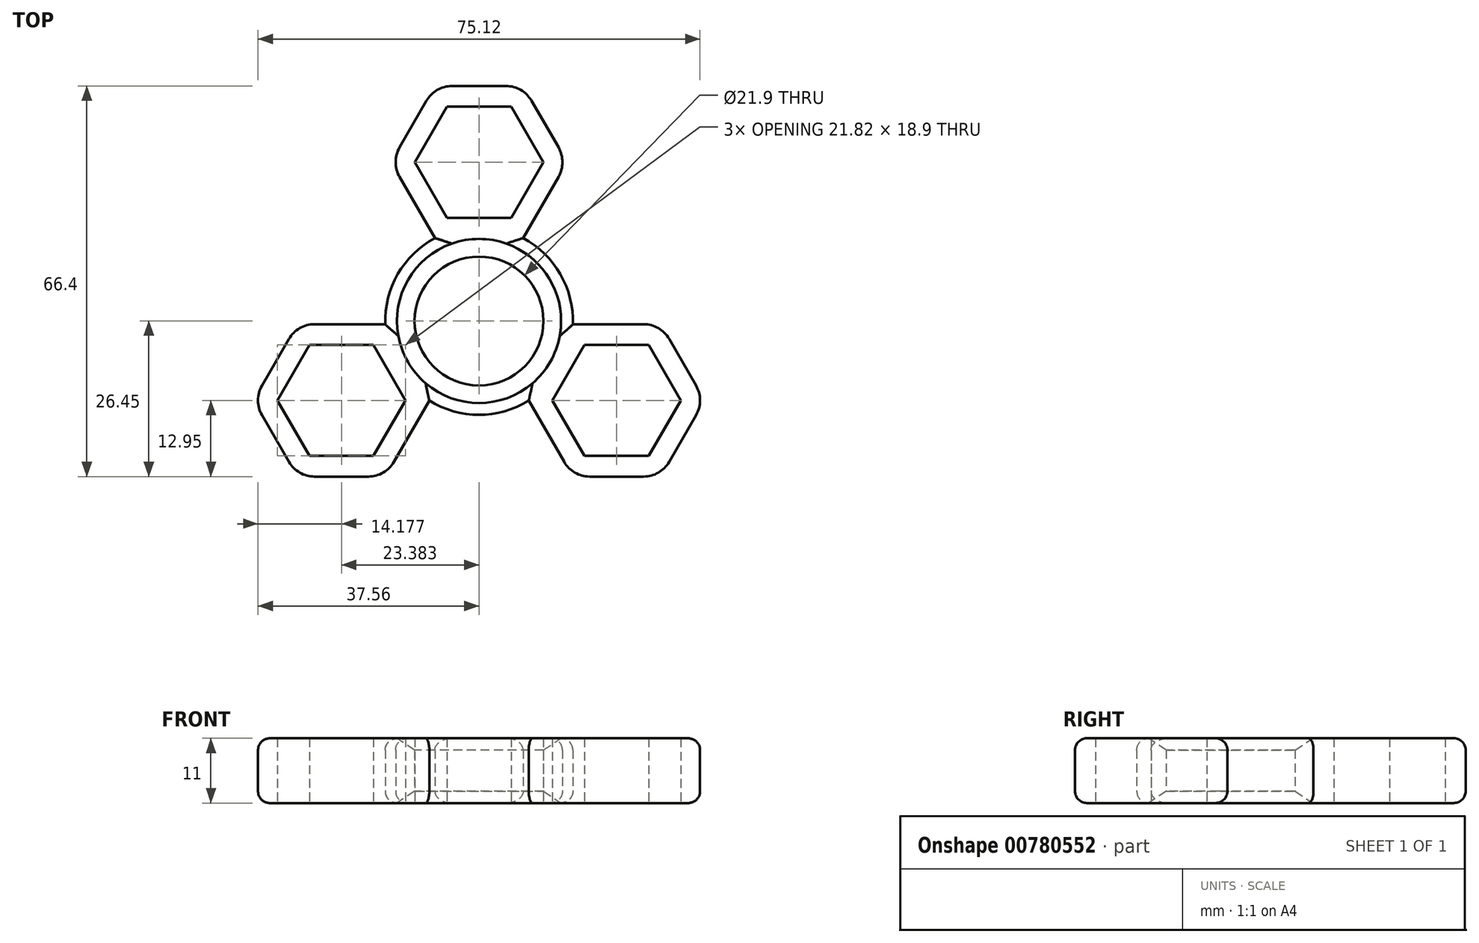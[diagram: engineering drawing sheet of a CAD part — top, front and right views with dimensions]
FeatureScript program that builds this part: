
annotation { "Feature Type Name" : "Feature", "Feature Type Description" : "" }
export const myFeature = defineFeature(function(context is Context, id is Id, definition is map)
    precondition{}
    {
        {
            var Q0;
            Q0=qCreatedBy(makeId("Top.planeOp"),FACE);
            var sketch = newSketch(context, id + "F0", { "sketchPlane" : qUnion([Q0])});
            skCircle(sketch, "E0", {"center": v(0, 0) * mm, "radius": 10.95 * mm});
            skCircle(sketch, "E1.cCircle", {"center": v(0, 0) * mm, "radius": 13.5 * mm, "construction": true});
            skLineSegment(sketch, "E1.0", {"start": v(0, 27) * mm, "end": v(23.38, -13.5) * mm, "construction": true});
            skLineSegment(sketch, "E1.1", {"start": v(23.38, -13.5) * mm, "end": v(-23.38, -13.5) * mm, "construction": true});
            skLineSegment(sketch, "E1.2", {"start": v(-23.38, -13.5) * mm, "end": v(0, 27) * mm, "construction": true});
            skPoint(sketch, "E1.0.midPoint", {"position": v(11.7, 6.75) * mm});
            skLineSegment(sketch, "E2", {"start": v(0, 0) * mm, "end": v(-23.38, -13.5) * mm, "construction": true});
            skLineSegment(sketch, "E3", {"start": v(0, 0) * mm, "end": v(23.38, -13.5) * mm, "construction": true});
            skLineSegment(sketch, "E4", {"start": v(0, 0) * mm, "end": v(0, 27) * mm, "construction": true});
            skCircle(sketch, "E5.cCircle", {"center": v(0, 27) * mm, "radius": 9.45 * mm, "construction": true});
            skLineSegment(sketch, "E5.0", {"start": v(-5.46, 36.45) * mm, "end": v(5.46, 36.45) * mm});
            skLineSegment(sketch, "E5.1", {"start": v(5.46, 36.45) * mm, "end": v(10.91, 27) * mm});
            skLineSegment(sketch, "E5.2", {"start": v(10.91, 27) * mm, "end": v(5.46, 17.55) * mm});
            skLineSegment(sketch, "E5.3", {"start": v(5.46, 17.55) * mm, "end": v(-5.46, 17.55) * mm});
            skLineSegment(sketch, "E5.4", {"start": v(-5.46, 17.55) * mm, "end": v(-10.91, 27) * mm});
            skLineSegment(sketch, "E5.5", {"start": v(-10.91, 27) * mm, "end": v(-5.46, 36.45) * mm});
            skPoint(sketch, "E5.0.midPoint", {"position": v(0, 36.45) * mm});
            skCircle(sketch, "E6.cCircle", {"center": v(23.38, -13.5) * mm, "radius": 9.45 * mm, "construction": true});
            skLineSegment(sketch, "E6.0", {"start": v(34.3, -13.5) * mm, "end": v(28.84, -22.95) * mm});
            skLineSegment(sketch, "E6.1", {"start": v(28.84, -22.95) * mm, "end": v(17.93, -22.95) * mm});
            skLineSegment(sketch, "E6.2", {"start": v(17.93, -22.95) * mm, "end": v(12.47, -13.5) * mm});
            skLineSegment(sketch, "E6.3", {"start": v(12.47, -13.5) * mm, "end": v(17.93, -4.05) * mm});
            skLineSegment(sketch, "E6.4", {"start": v(17.93, -4.05) * mm, "end": v(28.84, -4.05) * mm});
            skLineSegment(sketch, "E6.5", {"start": v(28.84, -4.05) * mm, "end": v(34.3, -13.5) * mm});
            skPoint(sketch, "E6.0.midPoint", {"position": v(31.57, -18.22) * mm});
            skCircle(sketch, "E7.cCircle", {"center": v(-23.38, -13.5) * mm, "radius": 9.45 * mm, "construction": true});
            skLineSegment(sketch, "E7.0", {"start": v(-28.84, -22.95) * mm, "end": v(-34.3, -13.5) * mm});
            skLineSegment(sketch, "E7.1", {"start": v(-34.3, -13.5) * mm, "end": v(-28.84, -4.05) * mm});
            skLineSegment(sketch, "E7.2", {"start": v(-28.84, -4.05) * mm, "end": v(-17.93, -4.05) * mm});
            skLineSegment(sketch, "E7.3", {"start": v(-17.93, -4.05) * mm, "end": v(-12.47, -13.5) * mm});
            skLineSegment(sketch, "E7.4", {"start": v(-12.47, -13.5) * mm, "end": v(-17.93, -22.95) * mm});
            skLineSegment(sketch, "E7.5", {"start": v(-17.93, -22.95) * mm, "end": v(-28.84, -22.95) * mm});
            skPoint(sketch, "E7.0.midPoint", {"position": v(-31.57, -18.22) * mm});
            skLineSegment(sketch, "E8.0", {"start": v(-14.95, 27) * mm, "end": v(-7.48, 39.95) * mm});
            skLineSegment(sketch, "E8.1", {"start": v(7.48, 39.95) * mm, "end": v(14.95, 27) * mm});
            skLineSegment(sketch, "E8.2", {"start": v(14.95, 27) * mm, "end": v(7.48, 14.05) * mm});
            skLineSegment(sketch, "E8.3", {"start": v(-7.48, 39.95) * mm, "end": v(7.48, 39.95) * mm});
            skLineSegment(sketch, "E8.4", {"start": v(7.48, 14.05) * mm, "end": v(-7.48, 14.05) * mm});
            skLineSegment(sketch, "E8.5", {"start": v(-7.48, 14.05) * mm, "end": v(-14.95, 27) * mm});
            skLineSegment(sketch, "E9.0", {"start": v(8.43, -13.5) * mm, "end": v(15.9, -0.55) * mm});
            skLineSegment(sketch, "E9.1", {"start": v(30.86, -0.55) * mm, "end": v(38.34, -13.5) * mm});
            skLineSegment(sketch, "E9.2", {"start": v(38.34, -13.5) * mm, "end": v(30.86, -26.45) * mm});
            skLineSegment(sketch, "E9.3", {"start": v(15.9, -0.55) * mm, "end": v(30.86, -0.55) * mm});
            skLineSegment(sketch, "E9.4", {"start": v(30.86, -26.45) * mm, "end": v(15.9, -26.45) * mm});
            skLineSegment(sketch, "E9.5", {"start": v(15.9, -26.45) * mm, "end": v(8.43, -13.5) * mm});
            skLineSegment(sketch, "E10.0", {"start": v(-38.34, -13.5) * mm, "end": v(-30.86, -0.55) * mm});
            skLineSegment(sketch, "E10.1", {"start": v(-15.9, -0.55) * mm, "end": v(-8.43, -13.5) * mm});
            skLineSegment(sketch, "E10.2", {"start": v(-8.43, -13.5) * mm, "end": v(-15.9, -26.45) * mm});
            skLineSegment(sketch, "E10.3", {"start": v(-30.86, -0.55) * mm, "end": v(-15.9, -0.55) * mm});
            skLineSegment(sketch, "E10.4", {"start": v(-15.9, -26.45) * mm, "end": v(-30.86, -26.45) * mm});
            skLineSegment(sketch, "E10.5", {"start": v(-30.86, -26.45) * mm, "end": v(-38.34, -13.5) * mm});
            skCircle(sketch, "E11.0", {"center": v(0, 0) * mm, "radius": 15.95 * mm});
            skSolve(sketch);
        }
        {
            var Q0;
            Q0=qSketchRegion(id+"F0",true);
            extrude(context, id + "F1", {"entities" : qUnion([Q0]), "depth" : 11 * mm, "offsetDistance" : 25 * mm});
        }
        {
            var Q0;
            Q0=makeQuery(id+"F1.opExtrude","CAP_EDGE",EDGE,{"disambiguationData":[OSD([sQuery(id+"F0.wireOp",EDGE,"E8.5")])],"isStart":true});
            var Q1;
            {var subQ0=sQuery(id+"F0.wireOp",EDGE,"E11.0");Q1=makeQuery(id+"F1.opExtrude","CAP_EDGE",EDGE,{"disambiguationData":[OSD([subQ0]),TDD([makeQuery(id+"F0.imprint","IMPRINT",EDGE,{"disambiguationData":[TD([[makeQuery(id+"F0.imprint","INTERSECT",VERTEX,{"derivedFrom":[sQuery(id+"F0.wireOp",EDGE,"E8.5"),subQ0]}),-1.0]])],"derivedFrom":subQ0})])],"isStart":true});}
            var Q2;
            Q2=makeQuery(id+"F1.opExtrude","CAP_EDGE",EDGE,{"disambiguationData":[OSD([sQuery(id+"F0.wireOp",EDGE,"E10.3")])],"isStart":true});
            var Q3;
            Q3=makeQuery(id+"F1.opExtrude","CAP_EDGE",EDGE,{"disambiguationData":[OSD([sQuery(id+"F0.wireOp",EDGE,"E10.0")])],"isStart":true});
            var Q4;
            Q4=makeQuery(id+"F1.opExtrude","CAP_EDGE",EDGE,{"disambiguationData":[OSD([sQuery(id+"F0.wireOp",EDGE,"E10.5")])],"isStart":true});
            var Q5;
            Q5=makeQuery(id+"F1.opExtrude","CAP_EDGE",EDGE,{"disambiguationData":[OSD([sQuery(id+"F0.wireOp",EDGE,"E10.4")])],"isStart":true});
            var Q6;
            Q6=makeQuery(id+"F1.opExtrude","CAP_EDGE",EDGE,{"disambiguationData":[OSD([sQuery(id+"F0.wireOp",EDGE,"E10.2")])],"isStart":true});
            var Q7;
            {var subQ0=sQuery(id+"F0.wireOp",EDGE,"E11.0");Q7=makeQuery(id+"F1.opExtrude","CAP_EDGE",EDGE,{"disambiguationData":[OSD([subQ0]),TDD([makeQuery(id+"F0.imprint","IMPRINT",EDGE,{"disambiguationData":[TD([[makeQuery(id+"F0.imprint","INTERSECT",VERTEX,{"derivedFrom":[sQuery(id+"F0.wireOp",EDGE,"E9.5"),subQ0]}),1.0]])],"derivedFrom":subQ0})])],"isStart":true});}
            var Q8;
            Q8=makeQuery(id+"F1.opExtrude","CAP_EDGE",EDGE,{"disambiguationData":[OSD([sQuery(id+"F0.wireOp",EDGE,"E9.4")])],"isStart":true});
            var Q9;
            Q9=makeQuery(id+"F1.opExtrude","CAP_EDGE",EDGE,{"disambiguationData":[OSD([sQuery(id+"F0.wireOp",EDGE,"E9.2")])],"isStart":true});
            var Q10;
            Q10=makeQuery(id+"F1.opExtrude","CAP_EDGE",EDGE,{"disambiguationData":[OSD([sQuery(id+"F0.wireOp",EDGE,"E9.1")])],"isStart":true});
            var Q11;
            Q11=makeQuery(id+"F1.opExtrude","CAP_EDGE",EDGE,{"disambiguationData":[OSD([sQuery(id+"F0.wireOp",EDGE,"E9.3")])],"isStart":true});
            var Q12;
            {var subQ0=sQuery(id+"F0.wireOp",EDGE,"E11.0");Q12=makeQuery(id+"F1.opExtrude","CAP_EDGE",EDGE,{"disambiguationData":[OSD([subQ0]),TDD([makeQuery(id+"F0.imprint","IMPRINT",EDGE,{"disambiguationData":[TD([[makeQuery(id+"F0.imprint","INTERSECT",VERTEX,{"derivedFrom":[sQuery(id+"F0.wireOp",EDGE,"E8.2"),subQ0]}),1.0]])],"derivedFrom":subQ0})])],"isStart":true});}
            var Q13;
            Q13=makeQuery(id+"F1.opExtrude","CAP_EDGE",EDGE,{"disambiguationData":[OSD([sQuery(id+"F0.wireOp",EDGE,"E8.2")])],"isStart":true});
            var Q14;
            Q14=makeQuery(id+"F1.opExtrude","CAP_EDGE",EDGE,{"disambiguationData":[OSD([sQuery(id+"F0.wireOp",EDGE,"E8.1")])],"isStart":true});
            var Q15;
            Q15=makeQuery(id+"F1.opExtrude","CAP_EDGE",EDGE,{"disambiguationData":[OSD([sQuery(id+"F0.wireOp",EDGE,"E8.3")])],"isStart":true});
            var Q16;
            Q16=makeQuery(id+"F1.opExtrude","CAP_EDGE",EDGE,{"disambiguationData":[OSD([sQuery(id+"F0.wireOp",EDGE,"E8.0")])],"isStart":true});
            var Q17;
            Q17=makeQuery(id+"F1.opExtrude","CAP_EDGE",EDGE,{"disambiguationData":[OSD([sQuery(id+"F0.wireOp",EDGE,"E9.4")])],"isStart":false});
            var Q18;
            {var subQ0=sQuery(id+"F0.wireOp",EDGE,"E11.0");Q18=makeQuery(id+"F1.opExtrude","CAP_EDGE",EDGE,{"disambiguationData":[OSD([subQ0]),TDD([makeQuery(id+"F0.imprint","IMPRINT",EDGE,{"disambiguationData":[TD([[makeQuery(id+"F0.imprint","INTERSECT",VERTEX,{"derivedFrom":[sQuery(id+"F0.wireOp",EDGE,"E9.5"),subQ0]}),1.0]])],"derivedFrom":subQ0})])],"isStart":false});}
            var Q19;
            Q19=makeQuery(id+"F1.opExtrude","CAP_EDGE",EDGE,{"disambiguationData":[OSD([sQuery(id+"F0.wireOp",EDGE,"E9.5")])],"isStart":false});
            var Q20;
            Q20=makeQuery(id+"F1.opExtrude","CAP_EDGE",EDGE,{"disambiguationData":[OSD([sQuery(id+"F0.wireOp",EDGE,"E10.2")])],"isStart":false});
            var Q21;
            Q21=makeQuery(id+"F1.opExtrude","CAP_EDGE",EDGE,{"disambiguationData":[OSD([sQuery(id+"F0.wireOp",EDGE,"E10.4")])],"isStart":false});
            var Q22;
            Q22=makeQuery(id+"F1.opExtrude","CAP_EDGE",EDGE,{"disambiguationData":[OSD([sQuery(id+"F0.wireOp",EDGE,"E10.5")])],"isStart":false});
            var Q23;
            Q23=makeQuery(id+"F1.opExtrude","CAP_EDGE",EDGE,{"disambiguationData":[OSD([sQuery(id+"F0.wireOp",EDGE,"E10.0")])],"isStart":false});
            var Q24;
            Q24=makeQuery(id+"F1.opExtrude","CAP_EDGE",EDGE,{"disambiguationData":[OSD([sQuery(id+"F0.wireOp",EDGE,"E10.3")])],"isStart":false});
            var Q25;
            {var subQ0=sQuery(id+"F0.wireOp",EDGE,"E11.0");Q25=makeQuery(id+"F1.opExtrude","CAP_EDGE",EDGE,{"disambiguationData":[OSD([subQ0]),TDD([makeQuery(id+"F0.imprint","IMPRINT",EDGE,{"disambiguationData":[TD([[makeQuery(id+"F0.imprint","INTERSECT",VERTEX,{"derivedFrom":[sQuery(id+"F0.wireOp",EDGE,"E8.5"),subQ0]}),-1.0]])],"derivedFrom":subQ0})])],"isStart":false});}
            var Q26;
            Q26=makeQuery(id+"F1.opExtrude","CAP_EDGE",EDGE,{"disambiguationData":[OSD([sQuery(id+"F0.wireOp",EDGE,"E8.5")])],"isStart":false});
            var Q27;
            Q27=makeQuery(id+"F1.opExtrude","CAP_EDGE",EDGE,{"disambiguationData":[OSD([sQuery(id+"F0.wireOp",EDGE,"E8.0")])],"isStart":false});
            var Q28;
            Q28=makeQuery(id+"F1.opExtrude","CAP_EDGE",EDGE,{"disambiguationData":[OSD([sQuery(id+"F0.wireOp",EDGE,"E8.3")])],"isStart":false});
            var Q29;
            Q29=makeQuery(id+"F1.opExtrude","CAP_EDGE",EDGE,{"disambiguationData":[OSD([sQuery(id+"F0.wireOp",EDGE,"E8.1")])],"isStart":false});
            var Q30;
            Q30=makeQuery(id+"F1.opExtrude","CAP_EDGE",EDGE,{"disambiguationData":[OSD([sQuery(id+"F0.wireOp",EDGE,"E8.2")])],"isStart":false});
            var Q31;
            {var subQ0=sQuery(id+"F0.wireOp",EDGE,"E11.0");Q31=makeQuery(id+"F1.opExtrude","CAP_EDGE",EDGE,{"disambiguationData":[OSD([subQ0]),TDD([makeQuery(id+"F0.imprint","IMPRINT",EDGE,{"disambiguationData":[TD([[makeQuery(id+"F0.imprint","INTERSECT",VERTEX,{"derivedFrom":[sQuery(id+"F0.wireOp",EDGE,"E8.2"),subQ0]}),1.0]])],"derivedFrom":subQ0})])],"isStart":false});}
            var Q32;
            Q32=makeQuery(id+"F1.opExtrude","CAP_EDGE",EDGE,{"disambiguationData":[OSD([sQuery(id+"F0.wireOp",EDGE,"E9.3")])],"isStart":false});
            var Q33;
            Q33=makeQuery(id+"F1.opExtrude","CAP_EDGE",EDGE,{"disambiguationData":[OSD([sQuery(id+"F0.wireOp",EDGE,"E9.1")])],"isStart":false});
            var Q34;
            Q34=makeQuery(id+"F1.opExtrude","CAP_EDGE",EDGE,{"disambiguationData":[OSD([sQuery(id+"F0.wireOp",EDGE,"E9.2")])],"isStart":false});
            var Q35;
            Q35=makeQuery(id+"F1.opExtrude","CAP_EDGE",EDGE,{"disambiguationData":[OSD([sQuery(id+"F0.wireOp",EDGE,"E9.5")])],"isStart":true});
            fillet(context, id + "F2", {"entities" : qUnion([Q0, Q1, Q2, Q3, Q4, Q5, Q6, Q7, Q8, Q9, Q10, Q11, Q12, Q13, Q14, Q15, Q16, Q17, Q18, Q19, Q20, Q21, Q22, Q23, Q24, Q25, Q26, Q27, Q28, Q29, Q30, Q31, Q32, Q33, Q34, Q35]), "radius" : 2 * mm, "tangentPropagation" : true, "allowEdgeOverflow" : false});
        }
        {
            var Q0;
            Q0=makeQuery(id+"F1.opExtrude","SWEPT_EDGE",EDGE,{"disambiguationData":[OSD([sQuery(id+"F0.wireOp",EDGE,"E9.4"),sQuery(id+"F0.wireOp",EDGE,"E9.5")])]});
            var Q1;
            Q1=makeQuery(id+"F1.opExtrude","SWEPT_EDGE",EDGE,{"disambiguationData":[OSD([sQuery(id+"F0.wireOp",EDGE,"E9.2"),sQuery(id+"F0.wireOp",EDGE,"E9.4")])]});
            var Q2;
            Q2=makeQuery(id+"F1.opExtrude","SWEPT_EDGE",EDGE,{"disambiguationData":[OSD([sQuery(id+"F0.wireOp",EDGE,"E9.1"),sQuery(id+"F0.wireOp",EDGE,"E9.2")])]});
            var Q3;
            Q3=makeQuery(id+"F1.opExtrude","SWEPT_EDGE",EDGE,{"disambiguationData":[OSD([sQuery(id+"F0.wireOp",EDGE,"E9.1"),sQuery(id+"F0.wireOp",EDGE,"E9.3")])]});
            var Q4;
            Q4=makeQuery(id+"F1.opExtrude","SWEPT_EDGE",EDGE,{"disambiguationData":[OSD([sQuery(id+"F0.wireOp",EDGE,"E8.1"),sQuery(id+"F0.wireOp",EDGE,"E8.2")])]});
            var Q5;
            Q5=makeQuery(id+"F1.opExtrude","SWEPT_EDGE",EDGE,{"disambiguationData":[OSD([sQuery(id+"F0.wireOp",EDGE,"E8.1"),sQuery(id+"F0.wireOp",EDGE,"E8.3")])]});
            var Q6;
            Q6=makeQuery(id+"F1.opExtrude","SWEPT_EDGE",EDGE,{"disambiguationData":[OSD([sQuery(id+"F0.wireOp",EDGE,"E8.0"),sQuery(id+"F0.wireOp",EDGE,"E8.3")])]});
            var Q7;
            Q7=makeQuery(id+"F1.opExtrude","SWEPT_EDGE",EDGE,{"disambiguationData":[OSD([sQuery(id+"F0.wireOp",EDGE,"E8.0"),sQuery(id+"F0.wireOp",EDGE,"E8.5")])]});
            var Q8;
            Q8=makeQuery(id+"F1.opExtrude","SWEPT_EDGE",EDGE,{"disambiguationData":[OSD([sQuery(id+"F0.wireOp",EDGE,"E10.0"),sQuery(id+"F0.wireOp",EDGE,"E10.3")])]});
            var Q9;
            Q9=makeQuery(id+"F1.opExtrude","SWEPT_EDGE",EDGE,{"disambiguationData":[OSD([sQuery(id+"F0.wireOp",EDGE,"E10.0"),sQuery(id+"F0.wireOp",EDGE,"E10.5")])]});
            var Q10;
            Q10=makeQuery(id+"F1.opExtrude","SWEPT_EDGE",EDGE,{"disambiguationData":[OSD([sQuery(id+"F0.wireOp",EDGE,"E10.4"),sQuery(id+"F0.wireOp",EDGE,"E10.5")])]});
            var Q11;
            Q11=makeQuery(id+"F1.opExtrude","SWEPT_EDGE",EDGE,{"disambiguationData":[OSD([sQuery(id+"F0.wireOp",EDGE,"E10.2"),sQuery(id+"F0.wireOp",EDGE,"E10.4")])]});
            fillet(context, id + "F3", {"entities" : qUnion([Q0, Q1, Q2, Q3, Q4, Q5, Q6, Q7, Q8, Q9, Q10, Q11]), "radius" : 5 * mm, "tangentPropagation" : true, "allowEdgeOverflow" : false});
        }
        {
            var Q0;
            Q0=makeQuery(id+"F1.opExtrude","CAP_EDGE",EDGE,{"disambiguationData":[OSD([sQuery(id+"F0.wireOp",EDGE,"E0")])],"isStart":true});
            var Q1;
            Q1=makeQuery(id+"F1.opExtrude","CAP_EDGE",EDGE,{"disambiguationData":[OSD([sQuery(id+"F0.wireOp",EDGE,"E0")])],"isStart":false});
            chamfer(context, id + "F4", {"entities" : qUnion([Q0, Q1]), "chamferType" : ChamferType.TWO_OFFSETS, "width1" : 3 * mm, "oppositeDirection" : false, "width2" : 2 * mm, "tangentPropagation" : true});
        }
    });
